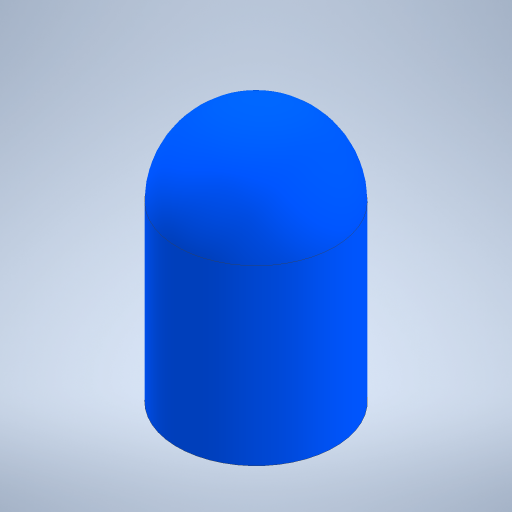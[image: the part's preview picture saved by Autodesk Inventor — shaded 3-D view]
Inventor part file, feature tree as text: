
AUTODESK INVENTOR PART (.ipt)
format: ipt  version: 2024.2 (Build 282272000, 272)  size: 240,640 bytes
history: native  units: mm
features: extrude x1, fillet x1, sketch x1
ambient origin geometry x8: Origin, YZ Plane, XZ Plane, XY Plane, X Axis, Y Axis, Z Axis, Center Point
bodies: Solid1 (feature_tree)
feature tree (3):
  extrude  "Extrusion1"  Depth=2.5mm TaperAngle=0.0deg
  fillet  "Fillet1"  Radius=2.5mm
  sketch  "Sketch1"  dims[d0=5.0mm d1=8.0mm d2=0.0mm d3=2.5mm]
